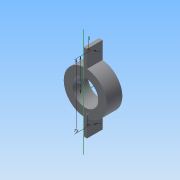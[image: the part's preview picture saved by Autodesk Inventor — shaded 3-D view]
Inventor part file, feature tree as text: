
AUTODESK INVENTOR PART (.ipt)
format: ipt  version: 2015 (Build 190159000, 159)  size: 98,816 bytes
history: native  units: mm
features: sketch x2, extrude x1
ambient origin geometry x8: Origin, YZ Plane, XZ Plane, XY Plane, X Axis, Y Axis, Z Axis, Center Point
bodies: Body1 (feature_tree)
feature tree (3):
  extrude  "Extrusion6"  Depth=40.0mm
  sketch  "Sketch5"  dims[d42=30.0mm d43=40.0mm d44=2.0mm d45=45.0mm d46=18.0mm d47=0.0mm d48=5.0mm d49=5.0mm d50=75.0mm d52=37.5mm]
  sketch  "Sketch4"  dims[d1=80.0mm d25=2.0mm d27=40.0mm]
